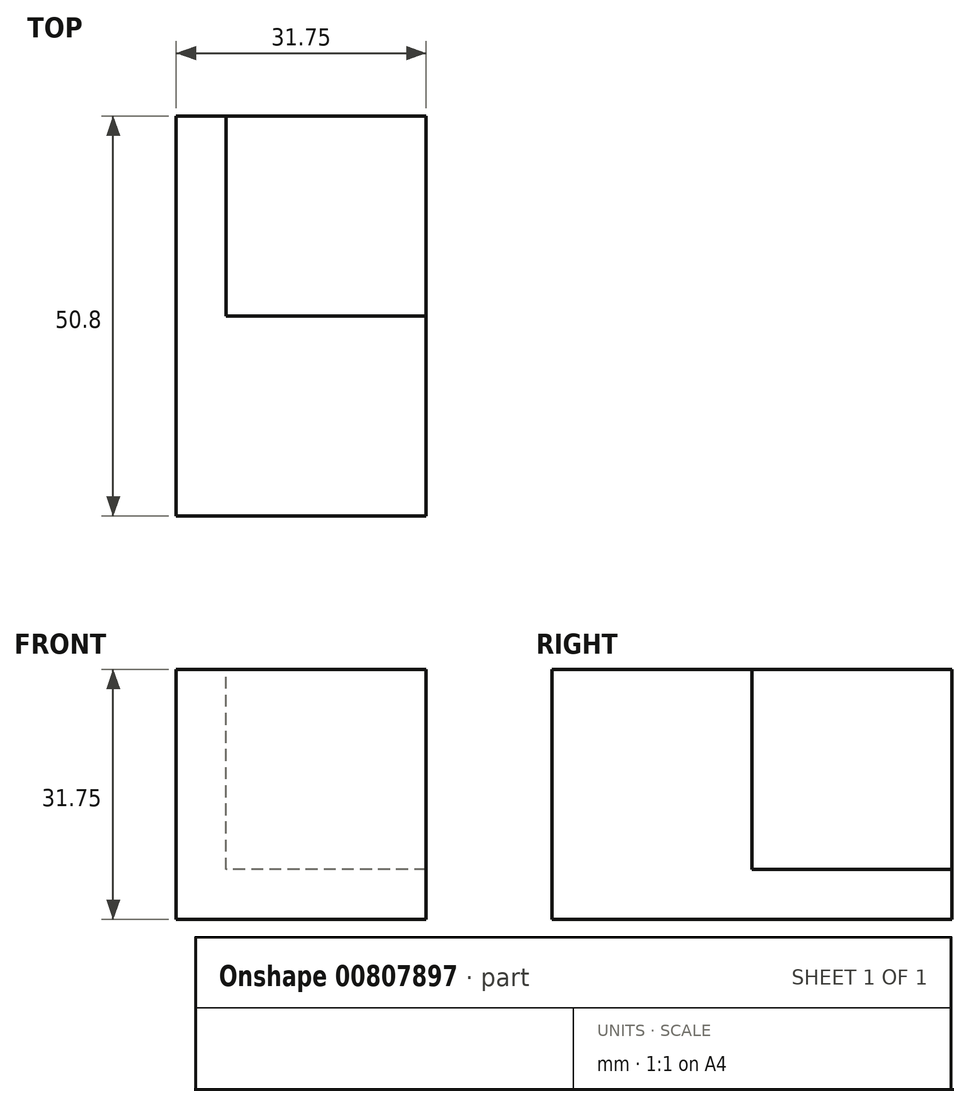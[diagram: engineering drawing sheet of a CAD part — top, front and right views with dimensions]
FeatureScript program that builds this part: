
annotation { "Feature Type Name" : "Feature", "Feature Type Description" : "" }
export const myFeature = defineFeature(function(context is Context, id is Id, definition is map)
    precondition{}
    {
        {
            var Q0;
            Q0=qCreatedBy(makeId("Right.planeOp"),FACE);
            var sketch = newSketch(context, id + "F0", { "sketchPlane" : qUnion([Q0])});
            skLineSegment(sketch, "E0.bottom", {"start": v(0, 0) * mm, "end": v(25.4, 0) * mm});
            skLineSegment(sketch, "E0.top", {"start": v(0, 31.75) * mm, "end": v(25.4, 31.75) * mm});
            skLineSegment(sketch, "E0.left", {"start": v(0, 0) * mm, "end": v(0, 31.75) * mm});
            skLineSegment(sketch, "E0.right", {"start": v(25.4, 0) * mm, "end": v(25.4, 31.75) * mm});
            skSolve(sketch);
        }
        {
            var Q0;
            Q0 = qSketchRegion(id + "F0", true);
            extrude(context, id + "F1", {"entities" : qUnion([Q0]), "depth" : 31.75 * mm, "offsetDistance" : 25.4 * mm});
        }
        {
            var Q0;
            Q0=makeQuery(id+"F1.opExtrude","SWEPT_FACE",FACE,{"disambiguationData":[OSD([sQuery(id+"F0.wireOp",EDGE,"E0.right")])]});
            var sketch = newSketch(context, id + "F2", { "sketchPlane" : qUnion([Q0])});
            skLineSegment(sketch, "E1.bottom", {"start": v(0, 0) * mm, "end": v(-6.35, 0) * mm});
            skLineSegment(sketch, "E1.top", {"start": v(0, 31.75) * mm, "end": v(-6.35, 31.75) * mm});
            skLineSegment(sketch, "E1.left", {"start": v(0, 0) * mm, "end": v(0, 31.75) * mm});
            skLineSegment(sketch, "E1.right", {"start": v(-6.35, 0) * mm, "end": v(-6.35, 31.75) * mm});
            skSolve(sketch);
        }
        {
            var Q0;
            Q0 = qSketchRegion(id + "F2", true);
            extrude(context, id + "F3", {"entities" : qUnion([Q0]), "operationType" : NewBodyOperationType.ADD, "depth" : 25.4 * mm, "offsetDistance" : 25.4 * mm});
        }
        {
            var Q0;
            Q0=makeQuery(id+"F3.opExtrude","SWEPT_FACE",FACE,{"disambiguationData":[OSD([sQuery(id+"F2.wireOp",EDGE,"E1.right")])]});
            var sketch = newSketch(context, id + "F4", { "sketchPlane" : qUnion([Q0])});
            skLineSegment(sketch, "E2.bottom", {"start": v(25.4, 6.33) * mm, "end": v(50.8, 6.33) * mm});
            skLineSegment(sketch, "E2.top", {"start": v(25.4, 0) * mm, "end": v(50.8, 0) * mm});
            skLineSegment(sketch, "E2.left", {"start": v(25.4, 6.33) * mm, "end": v(25.4, 0) * mm});
            skLineSegment(sketch, "E2.right", {"start": v(50.8, 6.33) * mm, "end": v(50.8, 0) * mm});
            skSolve(sketch);
        }
        {
            var Q0;
            Q0 = qSketchRegion(id + "F4", true);
            extrude(context, id + "F5", {"entities" : qUnion([Q0]), "operationType" : NewBodyOperationType.ADD, "depth" : 25.4 * mm, "offsetDistance" : 25.4 * mm});
        }
    });
